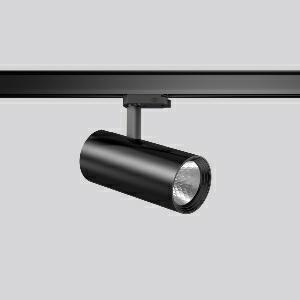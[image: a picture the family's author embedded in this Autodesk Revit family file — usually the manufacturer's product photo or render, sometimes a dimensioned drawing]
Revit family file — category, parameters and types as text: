
# Revit family: deecos_s_mini_742203_003_2_3e74
name_source: partatom
category: Lighting Fixtures
units: mm (PartAtom-declared; Revit-internal decimal feet)

## family parameters
Cut with Voids When Loaded = No
Host = Face
Light Source = No
Part Type = Normal
Room Calculation Point = No
Round Connector Dimension = Use Diameter
Shared = No

## types (1)
- DEECOS S mini (1 x LED Modul 927, 3400 lm, 2700)
    Apparent Load = 29 VA
    Approval mark = CE
    CIE Flux Codes = 100 100 100 100 100
    Color Rendering = 92
    Color Temperature = 2700
    Default Elevation = 1800 mm
    Description = Series: DEECOS S mini
LED surface-mounted projector in modern design with no visible cooling ribs. Housing: die-cast aluminium, powder-coated. Rotation range: 356°. Swivel range: 90°. Black plastic ring and recessed LED to prevent glare from the side. Optical assembly with reflector made of MIRO-Silver with 98% total light reflection for outstanding efficiency - can be changed without tools. Best colour rendering index Ra>90. With multi adaptor for 3-circuit tracks 230 V. Suitable for Track on ceiling, Wall track. High quality converter without flickering and stroboscopic effect. The following accessories can be mounted without use of tools: interchangeable lenses, decorative glasses, honeycomb louvre, clear and frosted diffusers, white interchangeable plastic ring. 
Colour: deep black, matt (RAL 9005)
Diameter: 87 mm
Height: 214 mm
Lamp: LED
Socket: without socket
Colour temperature: 2700K
Colour rendering index (CRI): 92
System power: 29 W
Rated luminous flux: 3400 lm
Luminous efficiency: 117 lm/W
Control gear: Regulated power supply
Protection class: I
Type of protection: IP 20
    Height = 214 mm
    Lamp = 1 x LED Modul 927
    Lamp Light Flux = 3400 lm
    Lamp count = 1
    Length = 87 mm
    Lifetime = 50000 h
    Luminous efficacy = 117 lm/W
    Manufacturer = RZB
    ModVariant = No
    Model = 742203.003.2
    Mounting Place = Ceiling
    Mounting Type = Rail mounted
    Number of Poles = 1
    OnlyDefault = Yes
    Power Factor = 1
    Product Name = DEECOS S mini
    Product group = Track mounted projectors
    ProductGroupID = 301
    Protection Class = Protection class I
    Protection Degree = IP 20
    RLX_Detail_Level = 1
    RLX_Emergency_Light_Flux = 0 lm
    RLX_Emergency_Type = 0
    RLX_Emergency_Type_DB = No
    RlxData = <blob elided: 38621 chars, md5=4ad4e096>
    Socket = socket
    Standby Power = 0 W
    System Light Flux = 3400 lm
    System Power = 29 W
    Type Comments = Product without accessories
    Type Image = 741926.003.jpg
    URL = http://relux.com
    VarID = ---
    Voltage = 230 V
    Voltage Range = 220-240 V
    Weight = 0.00 kg
    Width = 0 mm  [stored 0 ft]

note: [stored X ft] marks values corroborated as IEEE doubles in the binary element streams (Revit-internal decimal feet)

## geometry (parser evidence)
native form markers: Blend x4, Sweep x10
no freeform markers — native parametric forms only
